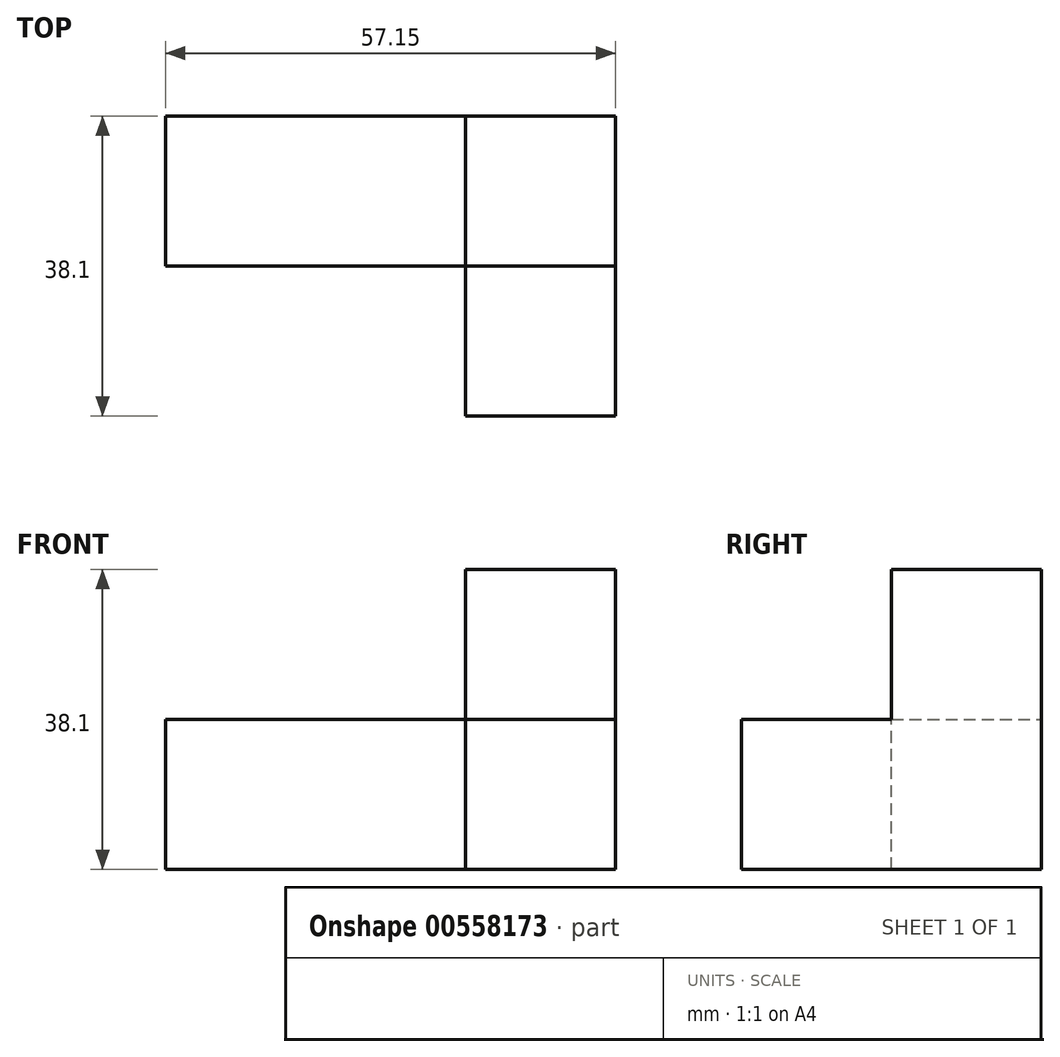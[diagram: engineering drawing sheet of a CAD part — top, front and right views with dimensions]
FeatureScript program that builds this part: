
annotation { "Feature Type Name" : "Feature", "Feature Type Description" : "" }
export const myFeature = defineFeature(function(context is Context, id is Id, definition is map)
    precondition{}
    {
        {
            var Q0;
            Q0=qCreatedBy(makeId("Front.planeOp"),FACE);
            var sketch = newSketch(context, id + "F0", { "sketchPlane" : qUnion([Q0])});
            skLineSegment(sketch, "E0", {"start": v(0, 0) * mm, "end": v(0, 19.05) * mm});
            skLineSegment(sketch, "E1", {"start": v(0, 19.05) * mm, "end": v(19.05, 19.05) * mm});
            skLineSegment(sketch, "E2", {"start": v(19.05, 19.05) * mm, "end": v(19.05, 0) * mm});
            skLineSegment(sketch, "E3", {"start": v(19.05, 0) * mm, "end": v(19.05, -19.05) * mm});
            skLineSegment(sketch, "E4", {"start": v(19.05, -19.05) * mm, "end": v(-38.1, -19.05) * mm});
            skLineSegment(sketch, "E5", {"start": v(-38.1, -19.05) * mm, "end": v(-38.1, 0) * mm});
            skLineSegment(sketch, "E6", {"start": v(-38.1, 0) * mm, "end": v(0, 0) * mm});
            skSolve(sketch);
        }
        {
            var Q0;
            Q0 = qSketchRegion(id + "F0", true);
            extrude(context, id + "F1", {"entities" : qUnion([Q0]), "depth" : 19.05 * mm, "offsetDistance" : 25.4 * mm});
        }
        {
            var Q0;
            Q0=makeQuery(id+"F1.opExtrude","CAP_FACE",FACE,{"disambiguationData":[OSD([sQuery(id+"F0.wireOp",EDGE,"E0"),sQuery(id+"F0.wireOp",EDGE,"E1"),sQuery(id+"F0.wireOp",EDGE,"E2"),sQuery(id+"F0.wireOp",EDGE,"E3"),sQuery(id+"F0.wireOp",EDGE,"E4"),sQuery(id+"F0.wireOp",EDGE,"E5"),sQuery(id+"F0.wireOp",EDGE,"E6")])],"isStart":false});
            var sketch = newSketch(context, id + "F2", { "sketchPlane" : qUnion([Q0])});
            skLineSegment(sketch, "E7", {"start": v(0, 0) * mm, "end": v(0, -19.05) * mm});
            skLineSegment(sketch, "E8", {"start": v(0, -19.05) * mm, "end": v(19.05, -19.05) * mm});
            skLineSegment(sketch, "E9", {"start": v(19.05, -19.05) * mm, "end": v(19.05, 0) * mm});
            skLineSegment(sketch, "E10", {"start": v(19.05, 0) * mm, "end": v(0, 0) * mm});
            skSolve(sketch);
        }
        {
            var Q0;
            Q0 = qSketchRegion(id + "F2", true);
            extrude(context, id + "F3", {"entities" : qUnion([Q0]), "operationType" : NewBodyOperationType.ADD, "depth" : 19.05 * mm, "offsetDistance" : 25.4 * mm});
        }
    });
